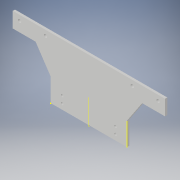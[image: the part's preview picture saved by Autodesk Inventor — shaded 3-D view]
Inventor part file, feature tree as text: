
AUTODESK INVENTOR PART (.ipt)
format: ipt  version: 2017 (Build 210142000, 142)  size: 142,336 bytes
history: native  units: in
note: dims shown in document units (in); Inventor stores cm internally (conversion verified against a paired STEP export)
features: sketch x11, hole x2, extrude x1, plane x1, mirror x1
ambient origin geometry x8: Origin, YZ Plane, XZ Plane, XY Plane, X Axis, Y Axis, Z Axis, Center Point
bodies: Solid1 (feature_tree)
feature tree (16):
  sketch  "Sketch1"  dims[d0=3.937in d1=7.874in]
  sketch  "Sketch2"  dims[d2=0.0in d3=0.7874in]
  sketch  "Sketch3"  dims[d4=1.1811in d5=1.1811in]
  sketch  "Sketch4"  dims[d6=0.7874in]
  extrude  "Extrusion1"  Depth=7.874in
  sketch  "Sketch6"  dims[d7=1.1811in]
  sketch  "Sketch7"  dims[d8=1.1811in]
  sketch  "Sketch8"  dims[d9=0.7874in]
  hole  "Hole2"  [1 undecoded]
  sketch  "Sketch11"  dims[d11=0.1181in d12=0.0in]
  hole  "Hole3"  [1 undecoded]
  plane  "Work Plane2"
  mirror  "Mirror1"
  sketch  "Sketch14"  dims[d38=0.5906in d39=0.2756in d40=0.3543in d42=0.1339in d43=0.2362in d44=0.1575in d45=0.0787in d46=90.0deg d47=0.315in d48=0.8108in d50=0.3543in d51=1.3386in d52=0.2756in d53=0.2756in d54=0.1732in d55=0.2362in d56=0.1575in d57=0.0787in d58=90.0deg d59=0.315in d60=0.8108in d62=-1.9685in]
  sketch  "Sketch9"  dims[d10=0.7874in]
  sketch  "Sketch12"  dims[d37=0.5906in]
note: 2 required parameter values undecoded (feature->parameter linkage not recoverable at this tier; creation-order binding heuristic only, values carry confidence <= 0.55)
